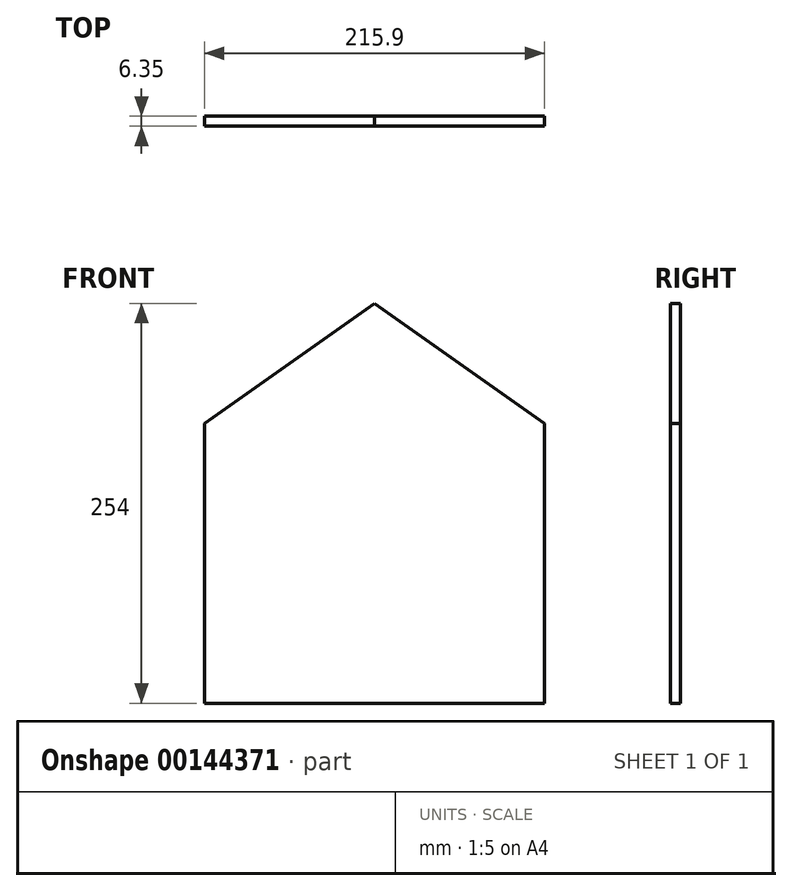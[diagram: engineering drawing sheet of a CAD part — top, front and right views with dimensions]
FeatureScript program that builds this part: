
annotation { "Feature Type Name" : "Feature", "Feature Type Description" : "" }
export const myFeature = defineFeature(function(context is Context, id is Id, definition is map)
    precondition{}
    {
        {
            var Q0;
            Q0=qCreatedBy(makeId("Front.planeOp"),FACE);
            var sketch = newSketch(context, id + "F0", { "sketchPlane" : qUnion([Q0])});
            skLineSegment(sketch, "E0.bottom", {"start": v(0, 0) * mm, "end": v(215.9, 0) * mm});
            skLineSegment(sketch, "E0.top", {"start": v(0, 177.8) * mm, "end": v(215.9, 177.8) * mm});
            skLineSegment(sketch, "E0.left", {"start": v(0, 0) * mm, "end": v(0, 177.8) * mm});
            skLineSegment(sketch, "E0.right", {"start": v(215.9, 0) * mm, "end": v(215.9, 177.8) * mm});
            skLineSegment(sketch, "E1", {"start": v(215.9, 177.8) * mm, "end": v(107.95, 254) * mm});
            skLineSegment(sketch, "E2", {"start": v(107.95, 254) * mm, "end": v(0, 177.8) * mm});
            skLineSegment(sketch, "E3", {"start": v(107.95, 254) * mm, "end": v(107.95, 177.8) * mm, "construction": true});
            skSolve(sketch);
        }
        {
            var Q0;
            Q0 = qSketchRegion(id + "F0", true);
            extrude(context, id + "F1", {"entities" : qUnion([Q0]), "depth" : 6.35 * mm});
        }
    });
